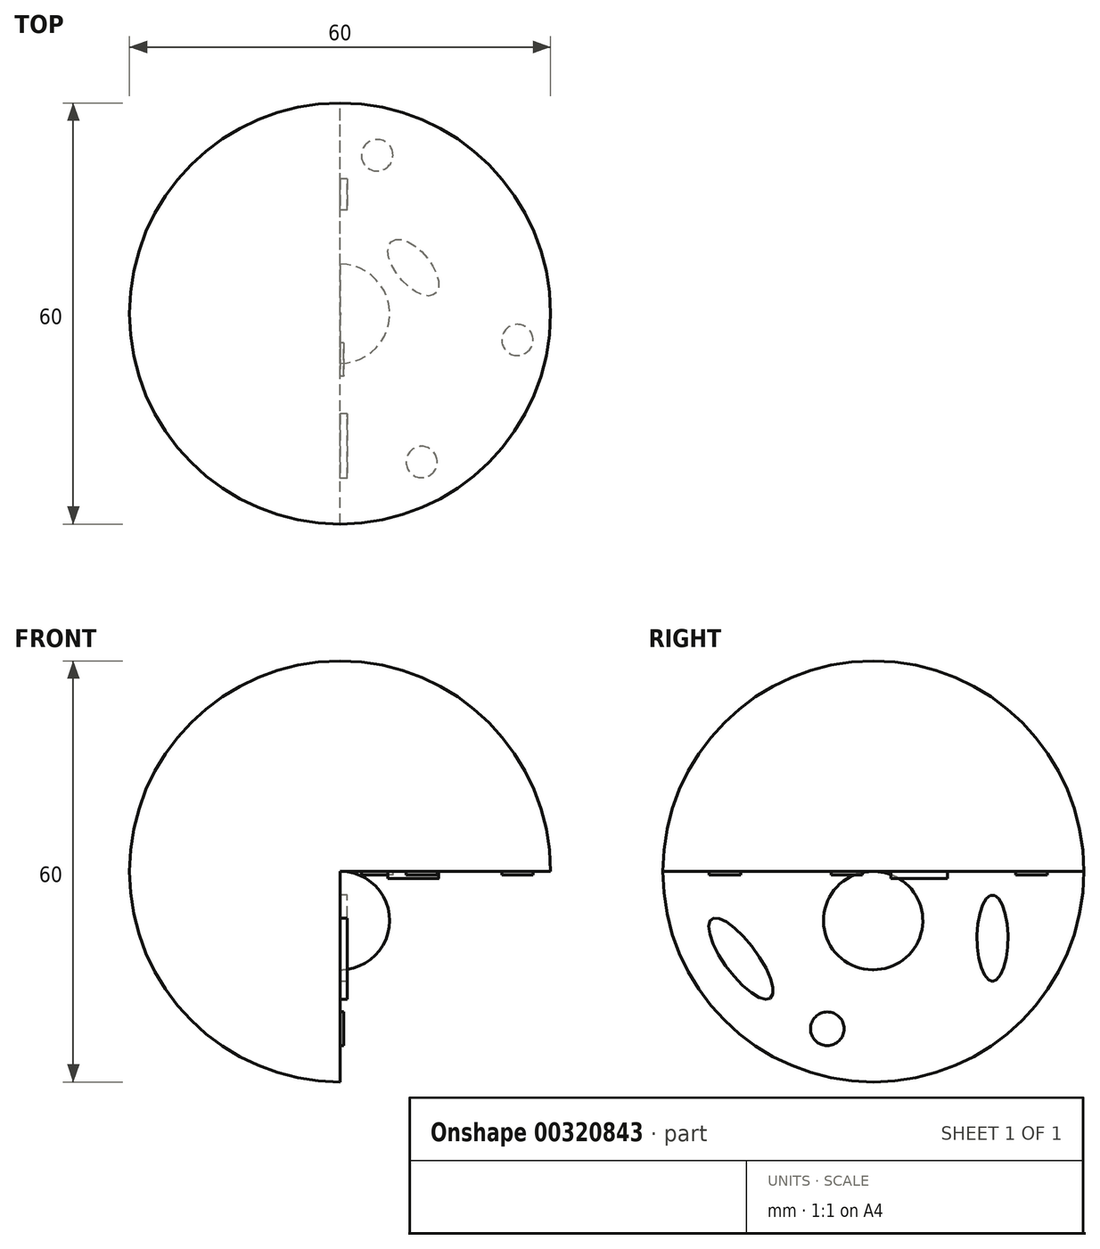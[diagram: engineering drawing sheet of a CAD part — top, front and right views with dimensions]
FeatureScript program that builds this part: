
annotation { "Feature Type Name" : "Feature", "Feature Type Description" : "" }
export const myFeature = defineFeature(function(context is Context, id is Id, definition is map)
    precondition{}
    {
        {
            var Q0;
            Q0=qCreatedBy(makeId("Right.planeOp"),FACE);
            var sketch = newSketch(context, id + "F0", { "sketchPlane" : qUnion([Q0])});
            skLineSegment(sketch, "E0", {"start": v(-29.97, 0) * mm, "end": v(30.03, 0) * mm});
            skArc(sketch, "E1", {"start": v(-29.97, 0) * mm, "mid": v(0.03, -30) * mm, "end": v(30.03, 0) * mm});
            skSolve(sketch);
        }
        {
            var Q0;
            Q0=makeQuery(id+"F0.imprint","IMPRINT",FACE,{"disambiguationData":[TD([[makeQuery(id+"F0.imprint","IMPRINT",EDGE,{"derivedFrom":sQuery(id+"F0.wireOp",EDGE,"E0")}),-1.0]])]});
            var Q1;
            Q1=sQuery(id+"F0.wireOp",EDGE,"E0");
            revolve(context, id + "F1", {"entities" : qUnion([Q0]), "axis" : qUnion([Q1]), "revolveType" : RevolveType.ONE_DIRECTION, "angle" : 270 * degree});
        }
        {
            var Q0;
            Q0=makeQuery(id+"F0.imprint","IMPRINT",FACE,{"disambiguationData":[TD([[makeQuery(id+"F0.imprint","IMPRINT",EDGE,{"derivedFrom":sQuery(id+"F0.wireOp",EDGE,"E0")}),-1.0]])]});
            var sketch = newSketch(context, id + "F2", { "sketchPlane" : qUnion([Q0])});
            skLineSegment(sketch, "E2", {"start": v(0, 0) * mm, "end": v(0, -14) * mm});
            skArc(sketch, "E3", {"start": v(0, 0) * mm, "mid": v(-7.08, -7) * mm, "end": v(0, -14) * mm});
            skSolve(sketch);
        }
        {
            var Q0;
            {var subQ0=sQuery(id+"F2.wireOp",EDGE,"E2");Q0=makeQuery(id+"F2.imprint","IMPRINT",FACE,{"disambiguationData":[TD([[makeQuery(id+"F2.imprint","IMPRINT",EDGE,{"derivedFrom":subQ0}),-1.0]])]});}
            var Q1;
            Q1 = qSketchRegion(id + "F2", true);
            var Q2;
            Q2=sQuery(id+"F2.wireOp",EDGE,"E2");
            revolve(context, id + "F3", {"operationType" : NewBodyOperationType.ADD, "entities" : qUnion([Q0, Q1]), "axis" : qUnion([Q2]), "revolveType" : RevolveType.FULL});
        }
        {
            var Q0;
            Q0=qCreatedBy(makeId("Right.planeOp"),FACE);
            var sketch = newSketch(context, id + "F4", { "sketchPlane" : qUnion([Q0])});
            skEllipse(sketch, "E4", {"center": v(17, -9.51) * mm, "majorRadius": 6.13 * mm, "minorRadius": 2.2 * mm, "majorAxis": v(0, -1)});
            skSolve(sketch);
        }
        {
            var Q0;
            Q0 = qSketchRegion(id + "F4", true);
            extrude(context, id + "F5", {"entities" : qUnion([Q0]), "operationType" : NewBodyOperationType.ADD, "depth" : 1 * mm});
        }
        {
            var Q0;
            Q0=qCreatedBy(makeId("Right.planeOp"),FACE);
            var sketch = newSketch(context, id + "F6", { "sketchPlane" : qUnion([Q0])});
            skEllipse(sketch, "E5", {"center": v(-18.85, -12.43) * mm, "majorRadius": 7.02 * mm, "minorRadius": 2.33 * mm, "majorAxis": v(0.6, -0.8)});
            skSolve(sketch);
        }
        {
            var Q0;
            Q0 = qSketchRegion(id + "F6", true);
            extrude(context, id + "F7", {"entities" : qUnion([Q0]), "operationType" : NewBodyOperationType.ADD, "depth" : 1 * mm});
        }
        {
            var Q0;
            Q0=makeQuery(id+"F1.opRevolve","CAP_FACE",FACE,{"disambiguationData":[OSD([sQuery(id+"F0.wireOp",EDGE,"E0"),sQuery(id+"F0.wireOp",EDGE,"E1")])],"isStart":true});
            var sketch = newSketch(context, id + "F8", { "sketchPlane" : qUnion([Q0])});
            skCircle(sketch, "E6", {"center": v(-6.53, -22.42) * mm, "radius": 2.4 * mm});
            skSolve(sketch);
        }
        {
            var Q0;
            Q0 = qSketchRegion(id + "F8", true);
            extrude(context, id + "F9", {"entities" : qUnion([Q0]), "operationType" : NewBodyOperationType.ADD, "depth" : 0.5 * mm});
        }
        {
            var Q0;
            Q0=makeQuery(id+"F1.opRevolve","CAP_FACE",FACE,{"disambiguationData":[OSD([sQuery(id+"F0.wireOp",EDGE,"E0"),sQuery(id+"F0.wireOp",EDGE,"E1")])],"isStart":false});
            var sketch = newSketch(context, id + "F10", { "sketchPlane" : qUnion([Q0])});
            skCircle(sketch, "E7", {"center": v(5.3, -22.6) * mm, "radius": 2.25 * mm});
            skSolve(sketch);
        }
        {
            var Q0;
            Q0 = qSketchRegion(id + "F10", true);
            extrude(context, id + "F11", {"entities" : qUnion([Q0]), "operationType" : NewBodyOperationType.ADD, "depth" : 0.5 * mm});
        }
        {
            var Q0;
            Q0=makeQuery(id+"F1.opRevolve","CAP_FACE",FACE,{"disambiguationData":[OSD([sQuery(id+"F0.wireOp",EDGE,"E0"),sQuery(id+"F0.wireOp",EDGE,"E1")])],"isStart":false});
            var sketch = newSketch(context, id + "F12", { "sketchPlane" : qUnion([Q0])});
            skCircle(sketch, "E8", {"center": v(25.28, 3.73) * mm, "radius": 2.22 * mm});
            skSolve(sketch);
        }
        {
            var Q0;
            Q0 = qSketchRegion(id + "F12", true);
            extrude(context, id + "F13", {"entities" : qUnion([Q0]), "operationType" : NewBodyOperationType.ADD, "depth" : 0.5 * mm});
        }
        {
            var Q0;
            Q0=makeQuery(id+"F1.opRevolve","CAP_FACE",FACE,{"disambiguationData":[OSD([sQuery(id+"F0.wireOp",EDGE,"E0"),sQuery(id+"F0.wireOp",EDGE,"E1")])],"isStart":false});
            var sketch = newSketch(context, id + "F14", { "sketchPlane" : qUnion([Q0])});
            skCircle(sketch, "E9", {"center": v(11.64, 21.12) * mm, "radius": 2.23 * mm});
            skSolve(sketch);
        }
        {
            var Q0;
            Q0 = qSketchRegion(id + "F14", true);
            extrude(context, id + "F15", {"entities" : qUnion([Q0]), "operationType" : NewBodyOperationType.ADD, "depth" : 0.5 * mm});
        }
        {
            var Q0;
            Q0=makeQuery(id+"F1.opRevolve","CAP_FACE",FACE,{"disambiguationData":[OSD([sQuery(id+"F0.wireOp",EDGE,"E0"),sQuery(id+"F0.wireOp",EDGE,"E1")])],"isStart":true});
            var sketch = newSketch(context, id + "F16", { "sketchPlane" : qUnion([Q0])});
            skPoint(sketch, "E10.28.internal.snap0", {"position": v(0.03, -30) * mm});
            skFitSpline(sketch, "E10", {"points": [v(4.8, -29.62) * mm, v(7.3, -27.12) * mm, v(10.47, -25.79) * mm, v(9.24, -24.97) * mm, v(6.22, -25.08) * mm, v(3.36, -24.53) * mm, v(7.66, -23.36) * mm, v(12.05, -23.58) * mm, v(11.5, -21.42) * mm, v(7.91, -20.4) * mm, v(4.82, -21.24) * mm, v(1.8, -21.72) * mm, v(3.15, -19.21) * mm, v(12.39, -18.98) * mm, v(12.03, -17.11) * mm, v(5.54, -15.54) * mm, v(-1.58, -17.85) * mm, v(-1.52, -16.4) * mm, v(7.55, -14) * mm, v(5.4, -11.56) * mm, v(3.89, -12.87) * mm, v(4.84, -14) * mm, v(-2.62, -14) * mm, v(-2.54, -19.02) * mm, v(0, -19.15) * mm, v(4.37, -17.62) * mm, v(9.29, -17.59) * mm, v(3.49, -18.36) * mm, v(0.03, -21.07) * mm, v(1.57, -23.11) * mm, v(6.68, -21.8) * mm, v(9.33, -21.4) * mm, v(8.5, -22.38) * mm, v(1.72, -23.78) * mm, v(3.76, -25.97) * mm, v(6.87, -26.22) * mm, v(2.56, -29.9) * mm], "startDerivative": vector(70.7, 105.52) * mm, "endDerivative": vector(-201.63, -146.12) * mm});
            skSolve(sketch);
        }
        {
            var Q0;
            Q0=sQuery(id+"F16.wireOp",EDGE,"E10");
            extrude(context, id + "F17", {"bodyType" : ToolBodyType.SURFACE, "surfaceEntities" : qUnion([Q0]), "depth" : 0.4 * mm});
        }
        {
            var Q0;
            Q0=qCreatedBy(makeId("Top.planeOp"),FACE);
            var sketch = newSketch(context, id + "F18", { "sketchPlane" : qUnion([Q0])});
            skFitSpline(sketch, "E11", {"points": [v(19.2, -22.82) * mm, v(21.41, -14.42) * mm, v(16.14, -20.25) * mm, v(17.67, -8.93) * mm, v(9, -16.74) * mm, v(16.36, -3.9) * mm, v(3.78, -15.3) * mm, v(9.27, -1.87) * mm, v(2.07, -11.25) * mm, v(5.33, -1.38) * mm, v(1.17, -5.51) * mm, v(0, 0) * mm, v(1.3, -4.4) * mm, v(5, 0) * mm, v(6.47, -1.06) * mm, v(3.43, -8.53) * mm, v(10.2, 0) * mm, v(5.31, -12.86) * mm, v(15.4, -2.33) * mm, v(17.38, -4.16) * mm, v(14.32, -9.47) * mm, v(19.4, -7.16) * mm, v(18.17, -15.17) * mm, v(22.69, -12.22) * mm, v(22.73, -19.55) * mm], "startDerivative": vector(118.78, 326.82) * mm, "endDerivative": vector(-54.13, -293.95) * mm});
            skSolve(sketch);
        }
        {
            var Q0;
            Q0 = qBodyType(qCreatedBy(id + "F18" ,EDGE), BodyType.WIRE);
            var Q1;
            Q1=sQuery(id+"F18.wireOp",EDGE,"E11");
            extrude(context, id + "F19", {"bodyType" : ToolBodyType.SURFACE, "surfaceEntities" : qUnion([Q0, Q1]), "oppositeDirection" : true, "depth" : 0.4 * mm});
        }
        {
            var Q0;
            Q0=makeQuery(id+"F1.opRevolve","CAP_FACE",FACE,{"disambiguationData":[OSD([sQuery(id+"F0.wireOp",EDGE,"E0"),sQuery(id+"F0.wireOp",EDGE,"E1")])],"isStart":false});
            var sketch = newSketch(context, id + "F20", { "sketchPlane" : qUnion([Q0])});
            skEllipse(sketch, "E12", {"center": v(10.45, -6.57) * mm, "majorRadius": 4.86 * mm, "minorRadius": 2.42 * mm, "majorAxis": v(-0.64, -0.76)});
            skSolve(sketch);
        }
        {
            var Q0;
            Q0 = qSketchRegion(id + "F20", true);
            extrude(context, id + "F21", {"entities" : qUnion([Q0]), "operationType" : NewBodyOperationType.ADD, "depth" : 1 * mm});
        }
        {
            var Q0;
            Q0=qCreatedBy(makeId("Top.planeOp"),FACE);
            var sketch = newSketch(context, id + "F22", { "sketchPlane" : qUnion([Q0])});
            skEllipse(sketch, "E13", {"center": v(21.98, 13.78) * mm, "majorRadius": 9.24 * mm, "minorRadius": 1.51 * mm, "majorAxis": v(-0.52, 0.85)});
            skEllipse(sketch, "E14", {"center": v(18.68, 11.27) * mm, "majorRadius": 7.69 * mm, "minorRadius": 1.52 * mm, "majorAxis": v(-0.53, 0.85)});
            skEllipse(sketch, "E15", {"center": v(15.67, 8.8) * mm, "majorRadius": 5.25 * mm, "minorRadius": 1.56 * mm, "majorAxis": v(-0.52, 0.85)});
            skSolve(sketch);
        }
        {
            var Q0;
            Q0=sQuery(id+"F22.wireOp",EDGE,"E14");
            var Q1;
            Q1=sQuery(id+"F22.wireOp",EDGE,"E13");
            var Q2;
            Q2=sQuery(id+"F22.wireOp",EDGE,"E15");
            extrude(context, id + "F23", {"bodyType" : ToolBodyType.SURFACE, "surfaceEntities" : qUnion([Q0, Q1, Q2]), "oppositeDirection" : true, "depth" : 0.4 * mm});
        }
        {
            var Q0;
            Q0=makeQuery(id+"F7.opExtrude","CAP_FACE",FACE,{"disambiguationData":[OSD([sQuery(id+"F6.wireOp",EDGE,"E5")])],"isStart":false});
            var sketch = newSketch(context, id + "F24", { "sketchPlane" : qUnion([Q0])});
            skPoint(sketch, "E16.1.internal.snap0", {"position": v(-23.03, -6.8) * mm});
            skPoint(sketch, "E16.23.internal.snap0", {"position": v(-23.03, -6.8) * mm});
            skFitSpline(sketch, "E16", {"points": [v(-23.03, -6.8) * mm, v(-23.03, -8.94) * mm, v(-21.05, -8.1) * mm, v(-21.95, -10.53) * mm, v(-19.37, -9.58) * mm, v(-20.35, -12.86) * mm, v(-17.6, -12.26) * mm, v(-18.87, -15) * mm, v(-15.92, -14.04) * mm, v(-16.7, -17.03) * mm, v(-14.67, -18.07) * mm, v(-16.35, -17.08) * mm, v(-15.5, -14.37) * mm, v(-15.96, -13.53) * mm, v(-18.23, -14.62) * mm, v(-17, -12.27) * mm, v(-18.38, -11.95) * mm, v(-19.94, -12.57) * mm, v(-18.86, -9.75) * mm, v(-19.7, -9.24) * mm, v(-21.48, -10.16) * mm, v(-20.78, -7.94) * mm, v(-22.22, -8.21) * mm, v(-23.03, -8.53) * mm, v(-23.03, -6.8) * mm]});
            skSolve(sketch);
        }
        {
            var Q0;
            Q0=sQuery(id+"F24.wireOp",EDGE,"E16");
            extrude(context, id + "F25", {"bodyType" : ToolBodyType.SURFACE, "surfaceEntities" : qUnion([Q0]), "depth" : 0.1 * mm});
        }
        {
            var Q0;
            Q0=makeQuery(id+"F5.opExtrude","CAP_FACE",FACE,{"disambiguationData":[OSD([sQuery(id+"F4.wireOp",EDGE,"E4")])],"isStart":false});
            var sketch = newSketch(context, id + "F26", { "sketchPlane" : qUnion([Q0])});
            skFitSpline(sketch, "E17", {"points": [v(15.97, -14.91) * mm, v(18.35, -13.13) * mm, v(15.58, -11.77) * mm, v(18.83, -9.72) * mm, v(15.23, -8.8) * mm, v(18.6, -6.97) * mm, v(15.57, -6.22) * mm, v(17.84, -4.72) * mm, v(16.4, -3.62) * mm, v(17.4, -4.51) * mm, v(15.3, -5.65) * mm, v(15.84, -6.97) * mm, v(17.98, -7.13) * mm, v(15.22, -8.27) * mm, v(15.3, -9.37) * mm, v(18.08, -9.8) * mm, v(15.43, -11.3) * mm, v(15.54, -12.4) * mm, v(17.74, -13.3) * mm, v(15.97, -14.91) * mm]});
            skSolve(sketch);
        }
        {
            var Q0;
            Q0=sQuery(id+"F26.wireOp",EDGE,"E17");
            extrude(context, id + "F27", {"bodyType" : ToolBodyType.SURFACE, "surfaceEntities" : qUnion([Q0]), "depth" : 0.1 * mm});
        }
        {
            var Q0;
            Q0=makeQuery(id+"F21.opExtrude","CAP_FACE",FACE,{"disambiguationData":[OSD([sQuery(id+"F20.wireOp",EDGE,"E12")])],"isStart":false});
            var sketch = newSketch(context, id + "F28", { "sketchPlane" : qUnion([Q0])});
            skPoint(sketch, "E18.9.internal.snap0", {"position": v(13.58, -2.86) * mm});
            skPoint(sketch, "E18.10.internal.snap0", {"position": v(13.58, -2.86) * mm});
            skPoint(sketch, "E18.13.internal.snap0", {"position": v(13.58, -2.86) * mm});
            skFitSpline(sketch, "E18", {"points": [v(6.84, -9.4) * mm, v(8.98, -10.08) * mm, v(7.55, -7.85) * mm, v(9.85, -9.2) * mm, v(8.17, -6.18) * mm, v(11.32, -8.63) * mm, v(9.5, -4.87) * mm, v(12.45, -7.09) * mm, v(10.87, -3.63) * mm, v(13.58, -5.48) * mm, v(12.62, -2.86) * mm, v(13.58, -2.86) * mm, v(12.95, -3.32) * mm, v(13.58, -4.88) * mm, v(13.78, -5.65) * mm, v(11.36, -4.25) * mm, v(12.8, -6.68) * mm, v(12.55, -7.27) * mm, v(10.12, -5.76) * mm, v(11.62, -8.1) * mm, v(11.6, -8.88) * mm, v(9.06, -7.26) * mm, v(10.2, -9) * mm, v(9.88, -9.47) * mm, v(8.33, -8.6) * mm, v(9.22, -10.03) * mm, v(8.99, -10.5) * mm, v(6.84, -9.4) * mm]});
            skSolve(sketch);
        }
        {
            var Q0;
            Q0=sQuery(id+"F28.wireOp",EDGE,"E18");
            extrude(context, id + "F29", {"bodyType" : ToolBodyType.SURFACE, "surfaceEntities" : qUnion([Q0]), "depth" : 0.1 * mm});
        }
    });
